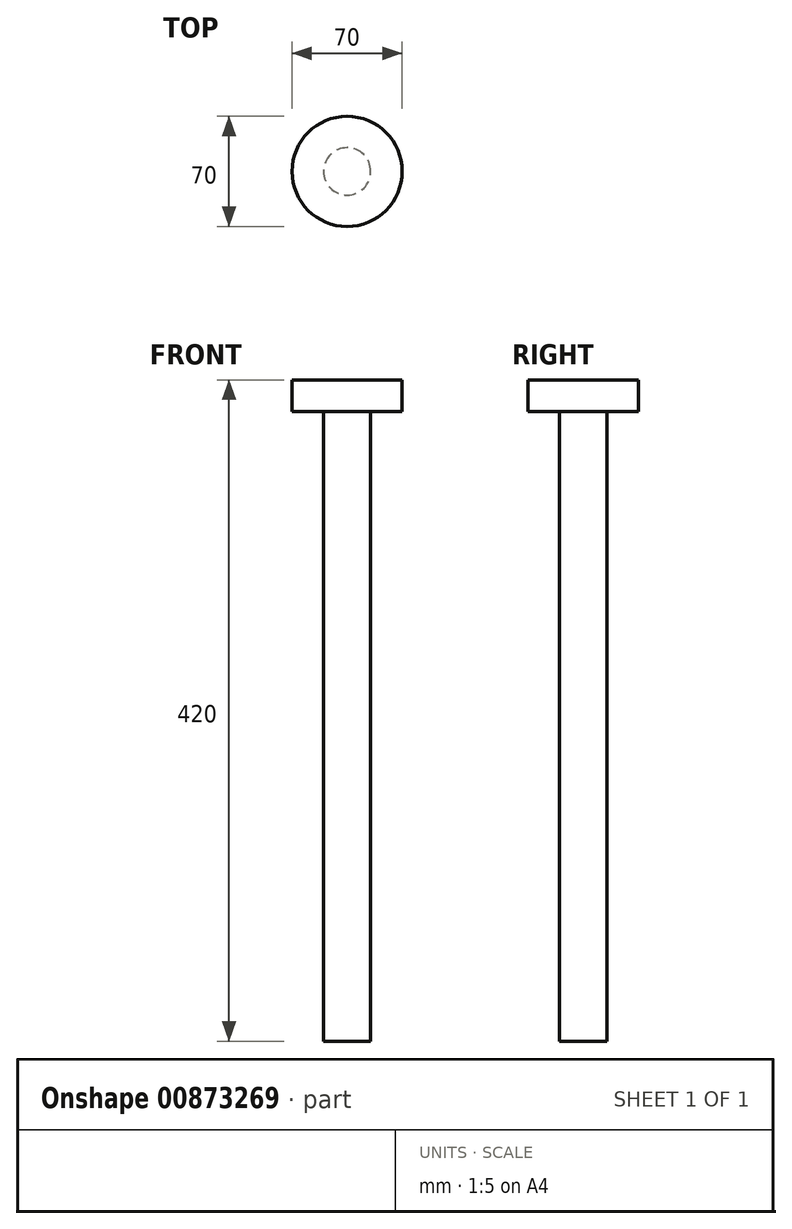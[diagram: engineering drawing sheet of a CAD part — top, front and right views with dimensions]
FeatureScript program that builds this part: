
annotation { "Feature Type Name" : "Feature", "Feature Type Description" : "" }
export const myFeature = defineFeature(function(context is Context, id is Id, definition is map)
    precondition{}
    {
        {
            var Q0;
            Q0=qCreatedBy(makeId("Front.planeOp"),FACE);
            var sketch = newSketch(context, id + "F0", { "sketchPlane" : qUnion([Q0])});
            skLineSegment(sketch, "E0", {"start": v(0, 185.21) * mm, "end": v(0, -173.02) * mm, "construction": true});
            skLineSegment(sketch, "E1", {"start": v(-15, 0) * mm, "end": v(-15, 400) * mm});
            skLineSegment(sketch, "E2", {"start": v(-35, 420) * mm, "end": v(0, 420) * mm});
            skLineSegment(sketch, "E3", {"start": v(-15, 0) * mm, "end": v(0, 0) * mm});
            skLineSegment(sketch, "E4", {"start": v(0, 420) * mm, "end": v(0, 0) * mm});
            skLineSegment(sketch, "E5", {"start": v(-15, 400) * mm, "end": v(-35, 400) * mm});
            skLineSegment(sketch, "E6", {"start": v(-35, 400) * mm, "end": v(-35, 420) * mm});
            skSolve(sketch);
        }
        {
            var Q0;
            Q0=makeQuery(id+"F0.imprint","IMPRINT",FACE,{"disambiguationData":[TD([[makeQuery(id+"F0.imprint","IMPRINT",EDGE,{"derivedFrom":sQuery(id+"F0.wireOp",EDGE,"E1")}),-1.0]])]});
            var Q1;
            Q1=sQuery(id+"F0.wireOp",EDGE,"E4");
            revolve(context, id + "F1", {"surfaceOperationType" : NewSurfaceOperationType.NEW, "entities" : qUnion([Q0]), "axis" : qUnion([Q1]), "revolveType" : RevolveType.FULL});
        }
    });
